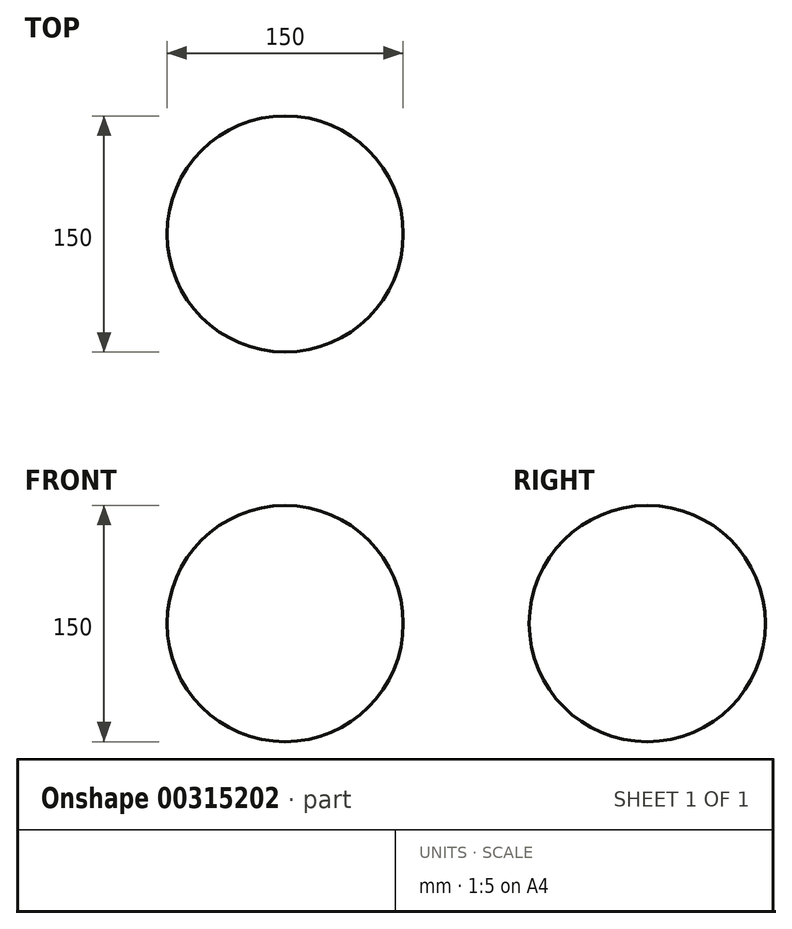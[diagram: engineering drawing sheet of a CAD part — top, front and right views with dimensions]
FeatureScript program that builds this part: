
annotation { "Feature Type Name" : "Feature", "Feature Type Description" : "" }
export const myFeature = defineFeature(function(context is Context, id is Id, definition is map)
    precondition{}
    {
        {
            var Q0;
            Q0=qCreatedBy(makeId("Front.planeOp"),FACE);
            var sketch = newSketch(context, id + "F0", { "sketchPlane" : qUnion([Q0])});
            skLineSegment(sketch, "E0", {"start": v(0, -75) * mm, "end": v(0, 75) * mm});
            skArc(sketch, "E1", {"start": v(0, 75) * mm, "mid": v(-75, 0) * mm, "end": v(0, -75) * mm});
            skLineSegment(sketch, "E2", {"start": v(0, 0) * mm, "end": v(-75, 0) * mm});
            skSolve(sketch);
        }
        {
            var Q0;
            {var subQ3=sQuery(id+"F0.wireOp",EDGE,"E2");Q0=makeQuery(id+"F0.imprint","IMPRINT",FACE,{"disambiguationData":[TD([[makeQuery(id+"F0.imprint","IMPRINT",EDGE,{"derivedFrom":subQ3}),1.0]])]});}
            var Q1;
            {var subQ3=sQuery(id+"F0.wireOp",EDGE,"E2");Q1=makeQuery(id+"F0.imprint","IMPRINT",FACE,{"disambiguationData":[TD([[makeQuery(id+"F0.imprint","IMPRINT",EDGE,{"derivedFrom":subQ3}),-1.0]])]});}
            var Q2;
            Q2=sQuery(id+"F0.wireOp",EDGE,"E0");
            revolve(context, id + "F1", {"entities" : qUnion([Q0, Q1]), "axis" : qUnion([Q2]), "revolveType" : RevolveType.FULL});
        }
    });
